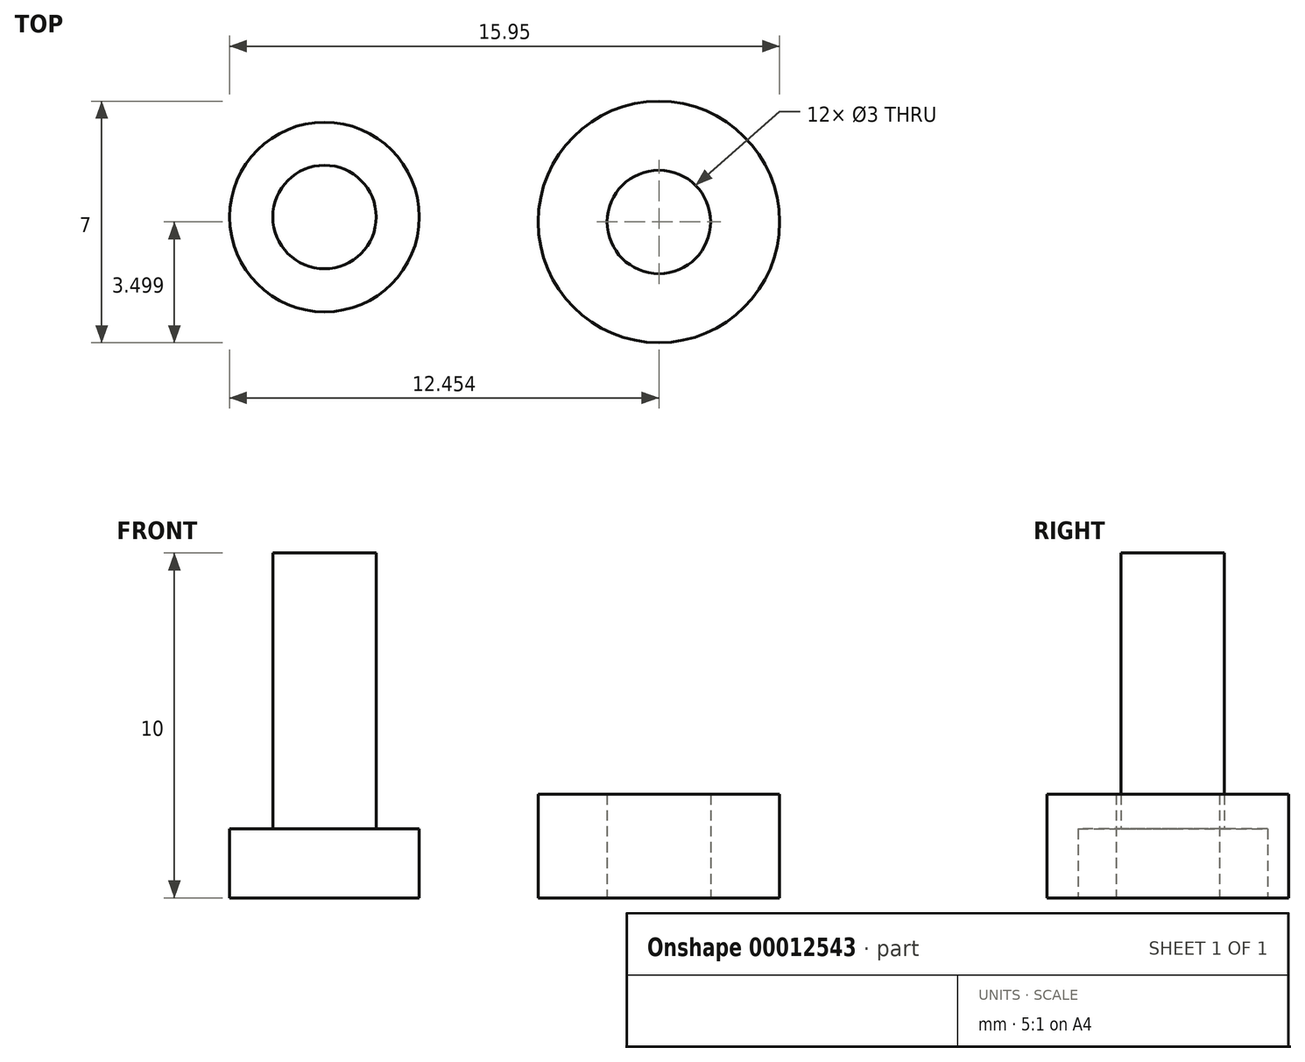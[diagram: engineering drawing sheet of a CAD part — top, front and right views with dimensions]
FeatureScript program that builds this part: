
annotation { "Feature Type Name" : "Feature", "Feature Type Description" : "" }
export const myFeature = defineFeature(function(context is Context, id is Id, definition is map)
    precondition{}
    {
        {
            var Q0;
            Q0=qCreatedBy(makeId("Top.planeOp"),FACE);
            var sketch = newSketch(context, id + "F0", { "sketchPlane" : qUnion([Q0])});
            skCircle(sketch, "E0", {"center": v(-55.82, 38.26) * mm, "radius": 1.5 * mm});
            skCircle(sketch, "E1", {"center": v(-55.82, 38.26) * mm, "radius": 2.75 * mm});
            skCircle(sketch, "E2", {"center": v(-46.12, 38.12) * mm, "radius": 3.5 * mm});
            skCircle(sketch, "E3", {"center": v(-46.12, 38.12) * mm, "radius": 1.5 * mm});
            skSolve(sketch);
        }
        {
            var Q0;
            Q0=makeQuery(id+"F0.imprint","IMPRINT",FACE,{"disambiguationData":[TD([[makeQuery(id+"F0.imprint","IMPRINT",EDGE,{"derivedFrom":sQuery(id+"F0.wireOp",EDGE,"E0")}),1.0]])]});
            extrude(context, id + "F1", {"entities" : qUnion([Q0]), "depth" : 10 * mm});
        }
        {
            var Q0;
            Q0=makeQuery(id+"F0.imprint","IMPRINT",FACE,{"disambiguationData":[TD([[makeQuery(id+"F0.imprint","IMPRINT",EDGE,{"derivedFrom":sQuery(id+"F0.wireOp",EDGE,"E0")}),-1.0]])]});
            extrude(context, id + "F2", {"entities" : qUnion([Q0]), "operationType" : NewBodyOperationType.ADD, "depth" : 2 * mm});
        }
        {
            var Q0;
            Q0=makeQuery(id+"F0.imprint","IMPRINT",FACE,{"disambiguationData":[TD([[makeQuery(id+"F0.imprint","IMPRINT",EDGE,{"derivedFrom":sQuery(id+"F0.wireOp",EDGE,"E2")}),1.0]])]});
            extrude(context, id + "F3", {"entities" : qUnion([Q0]), "depth" : 3 * mm});
        }
    });
